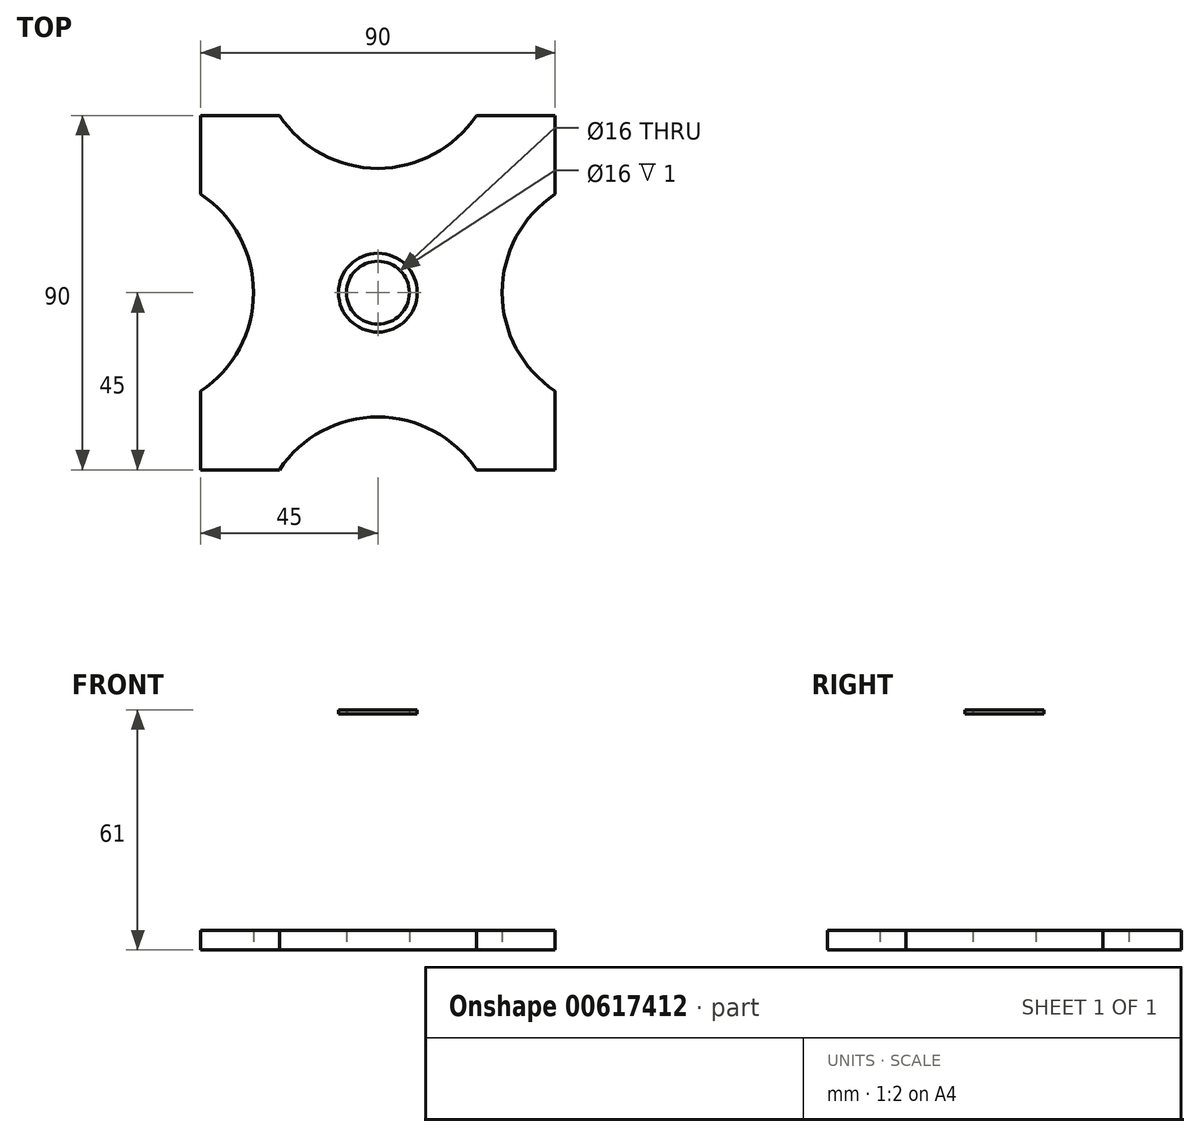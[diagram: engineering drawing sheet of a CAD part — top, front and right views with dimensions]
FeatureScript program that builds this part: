
annotation { "Feature Type Name" : "Feature", "Feature Type Description" : "" }
export const myFeature = defineFeature(function(context is Context, id is Id, definition is map)
    precondition{}
    {
        {
            var Q0;
            Q0=qCreatedBy(makeId("Top.planeOp"),FACE);
            var sketch = newSketch(context, id + "F0", { "sketchPlane" : qUnion([Q0])});
            skLineSegment(sketch, "E0.bottom", {"start": v(45, -45) * mm, "end": v(-45, -45) * mm});
            skLineSegment(sketch, "E0.top", {"start": v(45, 45) * mm, "end": v(-45, 45) * mm});
            skLineSegment(sketch, "E0.left", {"start": v(45, -45) * mm, "end": v(45, 45) * mm});
            skLineSegment(sketch, "E0.right", {"start": v(-45, -45) * mm, "end": v(-45, 45) * mm});
            skPoint(sketch, "E0.middle", {"position": v(0, 0) * mm});
            skArc(sketch, "E1", {"start": v(-45, -25) * mm, "mid": v(-31.58, 0) * mm, "end": v(-45, 25) * mm});
            skArc(sketch, "E2.MirrorCS", {"start": v(45, -25) * mm, "mid": v(31.58, 0) * mm, "end": v(45, 25) * mm});
            skArc(sketch, "E3", {"start": v(-25, 45) * mm, "mid": v(0, 31.58) * mm, "end": v(25, 45) * mm});
            skArc(sketch, "E4.MirrorCS", {"start": v(-25, -45) * mm, "mid": v(0, -31.58) * mm, "end": v(25, -45) * mm});
            skCircle(sketch, "E5", {"center": v(0, 0) * mm, "radius": 8 * mm});
            skSolve(sketch);
        }
        {
            var Q0;
            Q0=qCreatedBy(makeId("Top.planeOp"),FACE);
            cPlane(context, id + "F1", {"entities" : qUnion([Q0]), "cplaneType" : CPlaneType.OFFSET, "offset" : 60 * mm, "width" : 150 * mm, "height" : 150 * mm});
        }
        {
            var Q0;
            Q0=qCreatedBy(id+"F1.planeOp",FACE);
            var sketch = newSketch(context, id + "F2", { "sketchPlane" : qUnion([Q0])});
            skCircle(sketch, "E6", {"center": v(0, 0) * mm, "radius": 8 * mm});
            skCircle(sketch, "E7", {"center": v(0, 0) * mm, "radius": 10 * mm});
            skSolve(sketch);
        }
        {
            var Q0;
            {var subQ0=sQuery(id+"F0.wireOp",EDGE,"E1");Q0=makeQuery(id+"F0.imprint","IMPRINT",FACE,{"disambiguationData":[TD([[makeQuery(id+"F0.imprint","IMPRINT",EDGE,{"derivedFrom":subQ0}),-1.0]])]});}
            extrude(context, id + "F3", {"entities" : qUnion([Q0]), "depth" : 5 * mm, "offsetDistance" : 25 * mm});
        }
        {
            var Q0;
            Q0=makeQuery(id+"F2.imprint","IMPRINT",FACE,{"disambiguationData":[TD([[makeQuery(id+"F2.imprint","IMPRINT",EDGE,{"derivedFrom":sQuery(id+"F2.wireOp",EDGE,"E6")}),-1.0]])]});
            extrude(context, id + "F4", {"entities" : qUnion([Q0]), "depth" : 1 * mm, "offsetDistance" : 25 * mm});
        }
    });
